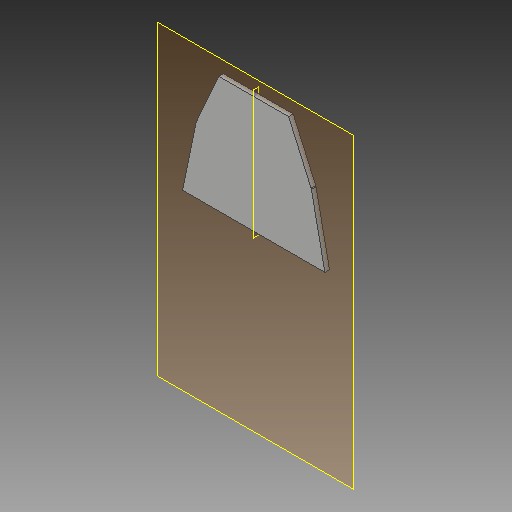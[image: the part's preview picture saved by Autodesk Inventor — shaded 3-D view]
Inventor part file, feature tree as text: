
AUTODESK INVENTOR PART (.ipt)
format: ipt  version: 2018 (Build 220112000, 112)  size: 173,056 bytes
history: native  units: mm
features: other x9, plane x1, sheet_metal_op x1, sketch x1, projected_geometry x1
ambient origin geometry x8: Origin, YZ Plane, XZ Plane, XY Plane, X Axis, Y Axis, Z Axis, Center Point
bodies: Solid1 (feature_tree)
feature tree (13):
  plane  "Work Plane1"
  sheet_metal_op  "Face1"
  other  "modplan parallel med plade"
  other  "midtplan"
  other  "Plate1"
  sketch  "Sketch3"  dims[d3=88.078826mm d4=44.039413mm d8=3.0mm d12=80.0mm d14=2.0mm d15=3.0mm d16=0.0mm]
  projected_geometry  "Projected Loop2"
  other  "2 mm mindre"
  other  "Definition1"
  parser-record x1  (decoder bookkeeping rows leaked as tree rows — omitted from the tree; the rows remain in map.json)
  other  "modul.iam"
  other  "stilladssøjle:1"
  other  "rør:1"
note: 1 file-system path scrubbed to <path> (originals preserved in map.json)
